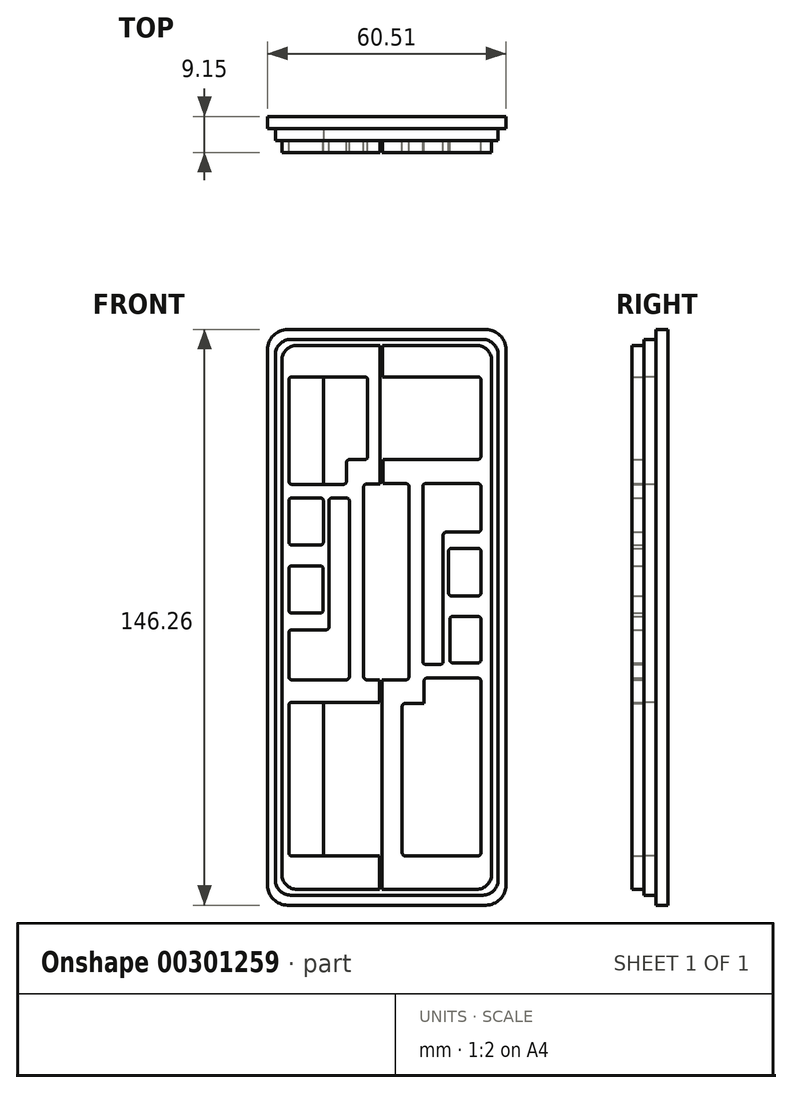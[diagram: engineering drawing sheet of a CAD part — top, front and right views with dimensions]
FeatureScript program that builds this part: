
annotation { "Feature Type Name" : "Feature", "Feature Type Description" : "" }
export const myFeature = defineFeature(function(context is Context, id is Id, definition is map)
    precondition{}
    {
        {
            var Q0;
            Q0=qCreatedBy(makeId("Front.planeOp"),FACE);
            var sketch = newSketch(context, id + "F0", { "sketchPlane" : qUnion([Q0])});
            skLineSegment(sketch, "E0", {"start": v(-27.22, -68.82) * mm, "end": v(-27.22, 61.78) * mm});
            skLineSegment(sketch, "E1", {"start": v(22.22, 65.6) * mm, "end": v(-23.4, 65.6) * mm});
            skLineSegment(sketch, "E2", {"start": v(22.22, -72.63) * mm, "end": v(-23.4, -72.63) * mm});
            skLineSegment(sketch, "E3", {"start": v(26.03, 61.78) * mm, "end": v(26.03, -68.82) * mm});
            skPoint(sketch, "E4.visualSharp", {"position": v(-27.22, 65.6) * mm});
            skArc(sketch, "E4.filletArc", {"start": v(-23.4, 65.6) * mm, "mid": v(-26.1, 64.48) * mm, "end": v(-27.22, 61.78) * mm});
            skPoint(sketch, "E5.visualSharp", {"position": v(26.03, 65.6) * mm});
            skArc(sketch, "E5.filletArc", {"start": v(26.03, 61.78) * mm, "mid": v(24.92, 64.48) * mm, "end": v(22.22, 65.6) * mm});
            skPoint(sketch, "E6.visualSharp", {"position": v(26.03, -72.63) * mm});
            skArc(sketch, "E6.filletArc", {"start": v(22.22, -72.63) * mm, "mid": v(24.92, -71.52) * mm, "end": v(26.03, -68.82) * mm});
            skPoint(sketch, "E7.visualSharp", {"position": v(-27.22, -72.63) * mm});
            skArc(sketch, "E7.filletArc", {"start": v(-27.22, -68.82) * mm, "mid": v(-26.1, -71.52) * mm, "end": v(-23.4, -72.63) * mm});
            skLineSegment(sketch, "E8", {"start": v(-24.7, -64.14) * mm, "end": v(-2.46, -64.14) * mm});
            skLineSegment(sketch, "E9", {"start": v(23.33, -63.38) * mm, "end": v(23.33, -19.72) * mm});
            skLineSegment(sketch, "E10", {"start": v(22.57, 57.59) * mm, "end": v(-1.65, 57.59) * mm});
            skLineSegment(sketch, "E11", {"start": v(-25.46, 56.82) * mm, "end": v(-25.46, 31.03) * mm});
            skLineSegment(sketch, "E12", {"start": v(-2.46, -25.08) * mm, "end": v(-24.7, -25.08) * mm});
            skLineSegment(sketch, "E13", {"start": v(-2.46, -25.08) * mm, "end": v(-2.46, -19.4) * mm});
            skLineSegment(sketch, "E14", {"start": v(-2.46, -19.4) * mm, "end": v(-5.7, -19.4) * mm});
            skLineSegment(sketch, "E15", {"start": v(-1.8, -19.4) * mm, "end": v(4.3, -19.4) * mm});
            skLineSegment(sketch, "E16", {"start": v(5.06, -18.63) * mm, "end": v(5.06, 29.68) * mm});
            skLineSegment(sketch, "E17", {"start": v(4.3, 30.44) * mm, "end": v(-1.52, 30.44) * mm});
            skLineSegment(sketch, "E18", {"start": v(-1.52, 30.44) * mm, "end": v(-1.52, 36.62) * mm});
            skLineSegment(sketch, "E19", {"start": v(-1.52, 36.62) * mm, "end": v(22.57, 36.62) * mm});
            skLineSegment(sketch, "E20", {"start": v(22.57, 30.47) * mm, "end": v(9.33, 30.47) * mm});
            skLineSegment(sketch, "E21", {"start": v(8.57, 29.71) * mm, "end": v(8.57, -14.73) * mm});
            skLineSegment(sketch, "E22", {"start": v(9.33, -15.49) * mm, "end": v(12.98, -15.49) * mm});
            skLineSegment(sketch, "E23", {"start": v(13.74, -14.73) * mm, "end": v(13.74, 17.36) * mm});
            skLineSegment(sketch, "E24", {"start": v(22.57, 14.02) * mm, "end": v(15.89, 14.02) * mm});
            skLineSegment(sketch, "E25", {"start": v(15.12, 13.26) * mm, "end": v(15.12, 2.68) * mm});
            skLineSegment(sketch, "E26", {"start": v(15.89, 1.92) * mm, "end": v(22.57, 1.92) * mm});
            skLineSegment(sketch, "E27", {"start": v(22.57, -3.28) * mm, "end": v(16.2, -3.28) * mm});
            skLineSegment(sketch, "E28", {"start": v(15.44, -4.04) * mm, "end": v(15.44, -14.33) * mm});
            skLineSegment(sketch, "E29", {"start": v(16.2, -15.1) * mm, "end": v(22.57, -15.1) * mm});
            skLineSegment(sketch, "E30", {"start": v(22.57, -18.96) * mm, "end": v(9.65, -18.96) * mm});
            skLineSegment(sketch, "E31", {"start": v(8.88, -19.72) * mm, "end": v(8.88, -25.38) * mm});
            skLineSegment(sketch, "E32", {"start": v(8.88, -25.38) * mm, "end": v(4.1, -25.38) * mm});
            skLineSegment(sketch, "E33", {"start": v(3.34, -26.14) * mm, "end": v(3.34, -63.38) * mm});
            skLineSegment(sketch, "E34", {"start": v(-1.8, -19.4) * mm, "end": v(-1.8, -72.63) * mm});
            skLineSegment(sketch, "E35", {"start": v(-2.46, -64.14) * mm, "end": v(-2.46, -72.63) * mm});
            skLineSegment(sketch, "E36.trimOffspring", {"start": v(4.1, -64.14) * mm, "end": v(22.57, -64.14) * mm});
            skLineSegment(sketch, "E37", {"start": v(-6.45, -18.63) * mm, "end": v(-6.45, 29.6) * mm});
            skLineSegment(sketch, "E38", {"start": v(-5.7, 30.36) * mm, "end": v(-2.29, 30.36) * mm});
            skLineSegment(sketch, "E39", {"start": v(-2.29, 30.36) * mm, "end": v(-2.29, 65.6) * mm});
            skLineSegment(sketch, "E40", {"start": v(-1.65, 65.6) * mm, "end": v(-1.65, 57.59) * mm});
            skPoint(sketch, "E40.endSnap0", {"position": v(-1.06, 57.59) * mm});
            skLineSegment(sketch, "E41.trimOffspring", {"start": v(-6.19, 57.59) * mm, "end": v(-24.7, 57.59) * mm});
            skLineSegment(sketch, "E42", {"start": v(-5.42, 56.82) * mm, "end": v(-5.42, 37.31) * mm});
            skLineSegment(sketch, "E43", {"start": v(-6.19, 36.55) * mm, "end": v(-10.06, 36.55) * mm});
            skLineSegment(sketch, "E44", {"start": v(-10.82, 35.79) * mm, "end": v(-10.82, 31.03) * mm});
            skLineSegment(sketch, "E45", {"start": v(-11.58, 30.27) * mm, "end": v(-24.7, 30.27) * mm});
            skLineSegment(sketch, "E46", {"start": v(-24.7, 26.82) * mm, "end": v(-17.45, 26.82) * mm});
            skLineSegment(sketch, "E47", {"start": v(-16.69, 26.06) * mm, "end": v(-16.69, 15.61) * mm});
            skLineSegment(sketch, "E48", {"start": v(-17.45, 14.85) * mm, "end": v(-24.7, 14.85) * mm});
            skLineSegment(sketch, "E49", {"start": v(-24.7, 9.56) * mm, "end": v(-17.51, 9.56) * mm});
            skLineSegment(sketch, "E50", {"start": v(-16.75, 8.8) * mm, "end": v(-16.75, -1.7) * mm});
            skLineSegment(sketch, "E51", {"start": v(-17.51, -2.46) * mm, "end": v(-24.7, -2.46) * mm});
            skLineSegment(sketch, "E52", {"start": v(-24.7, -6.7) * mm, "end": v(-16.03, -6.7) * mm});
            skLineSegment(sketch, "E53", {"start": v(-15.27, -5.94) * mm, "end": v(-15.27, 26.06) * mm});
            skLineSegment(sketch, "E54", {"start": v(-14.5, 26.82) * mm, "end": v(-10.86, 26.82) * mm});
            skLineSegment(sketch, "E55", {"start": v(-10.1, 26.06) * mm, "end": v(-10.1, -18.63) * mm});
            skLineSegment(sketch, "E56.trimOffspring", {"start": v(-10.86, -19.4) * mm, "end": v(-24.7, -19.4) * mm});
            skPoint(sketch, "E57.visualSharp", {"position": v(23.33, -64.14) * mm});
            skArc(sketch, "E57.filletArc", {"start": v(22.57, -64.14) * mm, "mid": v(23.1, -63.92) * mm, "end": v(23.33, -63.38) * mm});
            skPoint(sketch, "E58.visualSharp", {"position": v(3.34, -64.14) * mm});
            skArc(sketch, "E58.filletArc", {"start": v(3.34, -63.38) * mm, "mid": v(3.56, -63.92) * mm, "end": v(4.1, -64.14) * mm});
            skPoint(sketch, "E59.visualSharp", {"position": v(8.88, -18.96) * mm});
            skArc(sketch, "E59.filletArc", {"start": v(9.65, -18.96) * mm, "mid": v(9.1, -19.18) * mm, "end": v(8.88, -19.72) * mm});
            skPoint(sketch, "E60.newPointB", {"position": v(23.33, 57.59) * mm});
            skArc(sketch, "E60.filletArc", {"start": v(23.33, -19.72) * mm, "mid": v(23.1, -19.18) * mm, "end": v(22.57, -18.96) * mm});
            skPoint(sketch, "E61.visualSharp", {"position": v(3.34, -25.38) * mm});
            skArc(sketch, "E61.filletArc", {"start": v(4.1, -25.38) * mm, "mid": v(3.56, -25.6) * mm, "end": v(3.34, -26.14) * mm});
            skPoint(sketch, "E62.visualSharp", {"position": v(5.06, -19.4) * mm});
            skArc(sketch, "E62.filletArc", {"start": v(4.3, -19.4) * mm, "mid": v(4.84, -19.17) * mm, "end": v(5.06, -18.63) * mm});
            skPoint(sketch, "E63.visualSharp", {"position": v(8.57, -15.49) * mm});
            skArc(sketch, "E63.filletArc", {"start": v(8.57, -14.73) * mm, "mid": v(8.8, -15.26) * mm, "end": v(9.33, -15.49) * mm});
            skPoint(sketch, "E64.visualSharp", {"position": v(13.74, -15.49) * mm});
            skArc(sketch, "E64.filletArc", {"start": v(12.98, -15.49) * mm, "mid": v(13.51, -15.26) * mm, "end": v(13.74, -14.73) * mm});
            skPoint(sketch, "E65.visualSharp", {"position": v(15.44, -15.1) * mm});
            skArc(sketch, "E65.filletArc", {"start": v(15.44, -14.33) * mm, "mid": v(15.67, -14.87) * mm, "end": v(16.2, -15.1) * mm});
            skPoint(sketch, "E66.visualSharp", {"position": v(15.44, -3.28) * mm});
            skArc(sketch, "E66.filletArc", {"start": v(16.2, -3.28) * mm, "mid": v(15.67, -3.5) * mm, "end": v(15.44, -4.04) * mm});
            skPoint(sketch, "E67.visualSharp", {"position": v(15.12, 14.02) * mm});
            skArc(sketch, "E67.filletArc", {"start": v(15.89, 14.02) * mm, "mid": v(15.35, 13.8) * mm, "end": v(15.12, 13.26) * mm});
            skPoint(sketch, "E68.visualSharp", {"position": v(15.12, 1.92) * mm});
            skArc(sketch, "E68.filletArc", {"start": v(15.12, 2.68) * mm, "mid": v(15.35, 2.14) * mm, "end": v(15.89, 1.92) * mm});
            skPoint(sketch, "E69.visualSharp", {"position": v(8.57, 30.47) * mm});
            skArc(sketch, "E69.filletArc", {"start": v(9.33, 30.47) * mm, "mid": v(8.8, 30.25) * mm, "end": v(8.57, 29.71) * mm});
            skPoint(sketch, "E70.visualSharp", {"position": v(5.06, 30.44) * mm});
            skArc(sketch, "E70.filletArc", {"start": v(5.06, 29.68) * mm, "mid": v(4.84, 30.22) * mm, "end": v(4.3, 30.44) * mm});
            skPoint(sketch, "E71.visualSharp", {"position": v(-6.45, 30.36) * mm});
            skArc(sketch, "E71.filletArc", {"start": v(-5.7, 30.36) * mm, "mid": v(-6.23, 30.14) * mm, "end": v(-6.45, 29.6) * mm});
            skPoint(sketch, "E72.visualSharp", {"position": v(-10.1, 26.82) * mm});
            skArc(sketch, "E72.filletArc", {"start": v(-10.1, 26.06) * mm, "mid": v(-10.32, 26.6) * mm, "end": v(-10.86, 26.82) * mm});
            skPoint(sketch, "E73.visualSharp", {"position": v(-15.27, 26.82) * mm});
            skArc(sketch, "E73.filletArc", {"start": v(-14.5, 26.82) * mm, "mid": v(-15.04, 26.6) * mm, "end": v(-15.27, 26.06) * mm});
            skLineSegment(sketch, "E74", {"start": v(23.33, 56.82) * mm, "end": v(23.33, 37.38) * mm});
            skLineSegment(sketch, "E75.trimOffspring", {"start": v(23.33, -4.04) * mm, "end": v(23.33, -14.33) * mm});
            skLineSegment(sketch, "E76.trimOffspring", {"start": v(23.33, 29.71) * mm, "end": v(23.33, 18.88) * mm});
            skPoint(sketch, "E77.visualSharp", {"position": v(-16.69, 26.82) * mm});
            skArc(sketch, "E77.filletArc", {"start": v(-16.69, 26.06) * mm, "mid": v(-16.91, 26.6) * mm, "end": v(-17.45, 26.82) * mm});
            skPoint(sketch, "E78.visualSharp", {"position": v(-16.69, 14.85) * mm});
            skArc(sketch, "E78.filletArc", {"start": v(-17.45, 14.85) * mm, "mid": v(-16.91, 15.08) * mm, "end": v(-16.69, 15.61) * mm});
            skLineSegment(sketch, "E79.trimOffspring", {"start": v(-25.46, 8.8) * mm, "end": v(-25.46, -1.7) * mm});
            skLineSegment(sketch, "E80.trimOffspring", {"start": v(-25.46, 26.06) * mm, "end": v(-25.46, 15.61) * mm});
            skLineSegment(sketch, "E81.trimOffspring", {"start": v(-25.46, -7.46) * mm, "end": v(-25.46, -18.63) * mm});
            skLineSegment(sketch, "E82.trimOffspring", {"start": v(-25.46, -25.85) * mm, "end": v(-25.46, -63.38) * mm});
            skPoint(sketch, "E83.visualSharp", {"position": v(-25.46, -64.14) * mm});
            skArc(sketch, "E83.filletArc", {"start": v(-25.46, -63.38) * mm, "mid": v(-25.23, -63.92) * mm, "end": v(-24.7, -64.14) * mm});
            skPoint(sketch, "E84.visualSharp", {"position": v(-25.46, -25.08) * mm});
            skArc(sketch, "E84.filletArc", {"start": v(-24.7, -25.08) * mm, "mid": v(-25.23, -25.3) * mm, "end": v(-25.46, -25.85) * mm});
            skPoint(sketch, "E85.visualSharp", {"position": v(-6.45, -19.4) * mm});
            skArc(sketch, "E85.filletArc", {"start": v(-6.45, -18.63) * mm, "mid": v(-6.23, -19.17) * mm, "end": v(-5.7, -19.4) * mm});
            skPoint(sketch, "E86.visualSharp", {"position": v(-25.46, -19.4) * mm});
            skArc(sketch, "E86.filletArc", {"start": v(-25.46, -18.63) * mm, "mid": v(-25.23, -19.17) * mm, "end": v(-24.7, -19.4) * mm});
            skPoint(sketch, "E87.visualSharp", {"position": v(-10.1, -19.4) * mm});
            skArc(sketch, "E87.filletArc", {"start": v(-10.86, -19.4) * mm, "mid": v(-10.32, -19.17) * mm, "end": v(-10.1, -18.63) * mm});
            skPoint(sketch, "E88.visualSharp", {"position": v(-15.27, -6.7) * mm});
            skArc(sketch, "E88.filletArc", {"start": v(-16.03, -6.7) * mm, "mid": v(-15.49, -6.48) * mm, "end": v(-15.27, -5.94) * mm});
            skPoint(sketch, "E89.visualSharp", {"position": v(-25.46, -6.7) * mm});
            skArc(sketch, "E89.filletArc", {"start": v(-24.7, -6.7) * mm, "mid": v(-25.23, -6.92) * mm, "end": v(-25.46, -7.46) * mm});
            skPoint(sketch, "E90.visualSharp", {"position": v(-16.75, -2.46) * mm});
            skArc(sketch, "E90.filletArc", {"start": v(-17.51, -2.46) * mm, "mid": v(-16.97, -2.24) * mm, "end": v(-16.75, -1.7) * mm});
            skPoint(sketch, "E91.visualSharp", {"position": v(-25.46, -2.46) * mm});
            skArc(sketch, "E91.filletArc", {"start": v(-25.46, -1.7) * mm, "mid": v(-25.23, -2.24) * mm, "end": v(-24.7, -2.46) * mm});
            skPoint(sketch, "E92.visualSharp", {"position": v(-16.75, 9.56) * mm});
            skArc(sketch, "E92.filletArc", {"start": v(-16.75, 8.8) * mm, "mid": v(-16.97, 9.34) * mm, "end": v(-17.51, 9.56) * mm});
            skPoint(sketch, "E93.visualSharp", {"position": v(-25.46, 9.56) * mm});
            skArc(sketch, "E93.filletArc", {"start": v(-24.7, 9.56) * mm, "mid": v(-25.23, 9.34) * mm, "end": v(-25.46, 8.8) * mm});
            skPoint(sketch, "E94.visualSharp", {"position": v(-25.46, 14.85) * mm});
            skArc(sketch, "E94.filletArc", {"start": v(-25.46, 15.61) * mm, "mid": v(-25.23, 15.08) * mm, "end": v(-24.7, 14.85) * mm});
            skPoint(sketch, "E95.visualSharp", {"position": v(-25.46, 26.82) * mm});
            skArc(sketch, "E95.filletArc", {"start": v(-24.7, 26.82) * mm, "mid": v(-25.23, 26.6) * mm, "end": v(-25.46, 26.06) * mm});
            skPoint(sketch, "E96.visualSharp", {"position": v(-25.46, 57.59) * mm});
            skArc(sketch, "E96.filletArc", {"start": v(-24.7, 57.59) * mm, "mid": v(-25.23, 57.36) * mm, "end": v(-25.46, 56.82) * mm});
            skPoint(sketch, "E97.visualSharp", {"position": v(-5.42, 36.55) * mm});
            skArc(sketch, "E97.filletArc", {"start": v(-6.19, 36.55) * mm, "mid": v(-5.65, 36.77) * mm, "end": v(-5.42, 37.31) * mm});
            skPoint(sketch, "E98.visualSharp", {"position": v(-10.82, 30.27) * mm});
            skArc(sketch, "E98.filletArc", {"start": v(-11.58, 30.27) * mm, "mid": v(-11.04, 30.5) * mm, "end": v(-10.82, 31.03) * mm});
            skPoint(sketch, "E99.visualSharp", {"position": v(-25.46, 30.27) * mm});
            skArc(sketch, "E99.filletArc", {"start": v(-25.46, 31.03) * mm, "mid": v(-25.23, 30.5) * mm, "end": v(-24.7, 30.27) * mm});
            skPoint(sketch, "E100.visualSharp", {"position": v(-10.82, 36.55) * mm});
            skArc(sketch, "E100.filletArc", {"start": v(-10.06, 36.55) * mm, "mid": v(-10.6, 36.33) * mm, "end": v(-10.82, 35.79) * mm});
            skArc(sketch, "E101.filletArc", {"start": v(23.33, 56.82) * mm, "mid": v(23.1, 57.36) * mm, "end": v(22.57, 57.59) * mm});
            skPoint(sketch, "E102.visualSharp", {"position": v(23.33, 36.62) * mm});
            skArc(sketch, "E102.filletArc", {"start": v(22.57, 36.62) * mm, "mid": v(23.1, 36.84) * mm, "end": v(23.33, 37.38) * mm});
            skPoint(sketch, "E103.visualSharp", {"position": v(23.33, 30.47) * mm});
            skArc(sketch, "E103.filletArc", {"start": v(23.33, 29.71) * mm, "mid": v(23.1, 30.25) * mm, "end": v(22.57, 30.47) * mm});
            skPoint(sketch, "E104.visualSharp", {"position": v(23.33, 1.92) * mm});
            skArc(sketch, "E104.filletArc", {"start": v(22.57, 1.92) * mm, "mid": v(23.1, 2.14) * mm, "end": v(23.33, 2.68) * mm});
            skLineSegment(sketch, "E105", {"start": v(14.5, 18.12) * mm, "end": v(22.57, 18.12) * mm});
            skLineSegment(sketch, "E106.trimOffspring", {"start": v(23.33, 13.26) * mm, "end": v(23.33, 2.68) * mm});
            skPoint(sketch, "E107.visualSharp", {"position": v(-5.42, 57.59) * mm});
            skArc(sketch, "E107.filletArc", {"start": v(-5.42, 56.82) * mm, "mid": v(-5.65, 57.36) * mm, "end": v(-6.19, 57.59) * mm});
            skPoint(sketch, "E108.visualSharp", {"position": v(13.74, 18.12) * mm});
            skArc(sketch, "E108.filletArc", {"start": v(14.5, 18.12) * mm, "mid": v(13.96, 17.9) * mm, "end": v(13.74, 17.36) * mm});
            skPoint(sketch, "E109.visualSharp", {"position": v(23.33, 18.12) * mm});
            skArc(sketch, "E109.filletArc", {"start": v(22.57, 18.12) * mm, "mid": v(23.1, 18.34) * mm, "end": v(23.33, 18.88) * mm});
            skPoint(sketch, "E110.visualSharp", {"position": v(23.33, 14.02) * mm});
            skArc(sketch, "E110.filletArc", {"start": v(23.33, 13.26) * mm, "mid": v(23.1, 13.8) * mm, "end": v(22.57, 14.02) * mm});
            skPoint(sketch, "E111.visualSharp", {"position": v(23.33, -3.28) * mm});
            skArc(sketch, "E111.filletArc", {"start": v(23.33, -4.04) * mm, "mid": v(23.1, -3.5) * mm, "end": v(22.57, -3.28) * mm});
            skPoint(sketch, "E112.visualSharp", {"position": v(23.33, -15.1) * mm});
            skArc(sketch, "E112.filletArc", {"start": v(22.57, -15.1) * mm, "mid": v(23.1, -14.87) * mm, "end": v(23.33, -14.33) * mm});
            skSolve(sketch);
        }
        {
            var Q0;
            Q0=makeQuery(id+"F0.imprint","IMPRINT",FACE,{"disambiguationData":[TD([[makeQuery(id+"F0.imprint","IMPRINT",EDGE,{"derivedFrom":sQuery(id+"F0.wireOp",EDGE,"E0")}),-1.0]])]});
            var Q1;
            Q1=makeQuery(id+"F0.imprint","IMPRINT",FACE,{"disambiguationData":[TD([[makeQuery(id+"F0.imprint","IMPRINT",EDGE,{"derivedFrom":sQuery(id+"F0.wireOp",EDGE,"E3")}),-1.0]])]});
            extrude(context, id + "F1", {"entities" : qUnion([Q0, Q1]), "depth" : 3.05 * mm});
        }
        {
            var Q0;
            Q0=qCreatedBy(makeId("Front.planeOp"),FACE);
            var sketch = newSketch(context, id + "F2", { "sketchPlane" : qUnion([Q0])});
            skLineSegment(sketch, "E113.0", {"start": v(23.87, -74.1) * mm, "end": v(-25.06, -74.1) * mm});
            skLineSegment(sketch, "E113.1", {"start": v(23.87, 67.07) * mm, "end": v(-25.06, 67.07) * mm});
            skLineSegment(sketch, "E113.3", {"start": v(-28.87, -70.3) * mm, "end": v(-28.87, 63.26) * mm});
            skLineSegment(sketch, "E114", {"start": v(27.68, -70.3) * mm, "end": v(27.68, 63.26) * mm});
            skPoint(sketch, "E115.visualSharp", {"position": v(-28.87, -74.1) * mm});
            skArc(sketch, "E115.filletArc", {"start": v(-28.87, -70.3) * mm, "mid": v(-27.75, -72.99) * mm, "end": v(-25.06, -74.1) * mm});
            skPoint(sketch, "E116.visualSharp", {"position": v(27.68, -74.1) * mm});
            skArc(sketch, "E116.filletArc", {"start": v(23.87, -74.1) * mm, "mid": v(26.57, -72.99) * mm, "end": v(27.68, -70.3) * mm});
            skPoint(sketch, "E117.visualSharp", {"position": v(27.68, 67.07) * mm});
            skArc(sketch, "E117.filletArc", {"start": v(27.68, 63.26) * mm, "mid": v(26.57, 65.95) * mm, "end": v(23.87, 67.07) * mm});
            skPoint(sketch, "E118.visualSharp", {"position": v(-28.87, 67.07) * mm});
            skArc(sketch, "E118.filletArc", {"start": v(-25.06, 67.07) * mm, "mid": v(-27.75, 65.95) * mm, "end": v(-28.87, 63.26) * mm});
            skLineSegment(sketch, "E119.0", {"start": v(-24.7, -64.14) * mm, "end": v(-16.71, -64.14) * mm});
            skLineSegment(sketch, "E120.0", {"start": v(-25.46, -25.85) * mm, "end": v(-25.46, -63.38) * mm});
            skArc(sketch, "E120.1", {"start": v(-25.46, -63.38) * mm, "mid": v(-25.23, -63.92) * mm, "end": v(-24.7, -64.14) * mm});
            skArc(sketch, "E121.0", {"start": v(-24.7, -25.08) * mm, "mid": v(-25.23, -25.3) * mm, "end": v(-25.46, -25.85) * mm});
            skLineSegment(sketch, "E121.1", {"start": v(-16.71, -25.08) * mm, "end": v(-24.7, -25.08) * mm});
            skLineSegment(sketch, "E122.0", {"start": v(-16.71, 30.27) * mm, "end": v(-24.7, 30.27) * mm});
            skArc(sketch, "E122.1", {"start": v(-25.46, 31.03) * mm, "mid": v(-25.23, 30.5) * mm, "end": v(-24.7, 30.27) * mm});
            skLineSegment(sketch, "E122.2", {"start": v(-25.46, 56.82) * mm, "end": v(-25.46, 31.03) * mm});
            skLineSegment(sketch, "E122.3", {"start": v(-16.71, 57.59) * mm, "end": v(-24.7, 57.59) * mm});
            skArc(sketch, "E122.4", {"start": v(-24.7, 57.59) * mm, "mid": v(-25.23, 57.36) * mm, "end": v(-25.46, 56.82) * mm});
            skLineSegment(sketch, "E123", {"start": v(-16.71, 57.59) * mm, "end": v(-16.71, 30.27) * mm});
            skPoint(sketch, "E124.orphan", {"position": v(-2.46, -64.14) * mm});
            skPoint(sketch, "E125.orphan", {"position": v(-2.46, -25.08) * mm});
            skLineSegment(sketch, "E126.trimOffspring", {"start": v(-16.71, -25.08) * mm, "end": v(-16.71, -64.14) * mm});
            skPoint(sketch, "E127.orphan", {"position": v(-11.58, 30.27) * mm});
            skPoint(sketch, "E128.orphan", {"position": v(-6.19, 57.59) * mm});
            skSolve(sketch);
        }
        {
            var Q0;
            Q0 = qSketchRegion(id + "F2", true);
            extrude(context, id + "F3", {"entities" : qUnion([Q0]), "operationType" : NewBodyOperationType.ADD, "oppositeDirection" : true, "depth" : 3.05 * mm});
        }
        {
            var Q0;
            Q0=makeQuery(id+"F3.opExtrude","CAP_FACE",FACE,{"disambiguationData":[OSD([sQuery(id+"F2.wireOp",EDGE,"E113.0"),sQuery(id+"F2.wireOp",EDGE,"E113.1"),sQuery(id+"F2.wireOp",EDGE,"E113.3"),sQuery(id+"F2.wireOp",EDGE,"E114"),sQuery(id+"F2.wireOp",EDGE,"E115.filletArc"),sQuery(id+"F2.wireOp",EDGE,"E116.filletArc"),sQuery(id+"F2.wireOp",EDGE,"E117.filletArc"),sQuery(id+"F2.wireOp",EDGE,"E118.filletArc"),sQuery(id+"F2.wireOp",EDGE,"E119.0"),sQuery(id+"F2.wireOp",EDGE,"E120.0"),sQuery(id+"F2.wireOp",EDGE,"E120.1"),sQuery(id+"F2.wireOp",EDGE,"E121.0"),sQuery(id+"F2.wireOp",EDGE,"E121.1"),sQuery(id+"F2.wireOp",EDGE,"E122.0"),sQuery(id+"F2.wireOp",EDGE,"E122.1"),sQuery(id+"F2.wireOp",EDGE,"E122.2"),sQuery(id+"F2.wireOp",EDGE,"E122.3"),sQuery(id+"F2.wireOp",EDGE,"E122.4"),sQuery(id+"F2.wireOp",EDGE,"E123"),sQuery(id+"F2.wireOp",EDGE,"E126.trimOffspring")])],"isStart":false});
            var sketch = newSketch(context, id + "F4", { "sketchPlane" : qUnion([Q0])});
            skLineSegment(sketch, "E129", {"start": v(-29.66, -71.57) * mm, "end": v(-29.66, 64.53) * mm});
            skLineSegment(sketch, "E130", {"start": v(-24.58, 69.6) * mm, "end": v(25.77, 69.6) * mm});
            skLineSegment(sketch, "E131", {"start": v(30.85, 64.53) * mm, "end": v(30.85, -71.57) * mm});
            skLineSegment(sketch, "E132", {"start": v(25.77, -76.65) * mm, "end": v(-24.58, -76.65) * mm});
            skPoint(sketch, "E133.visualSharp", {"position": v(-29.66, 69.6) * mm});
            skArc(sketch, "E133.filletArc", {"start": v(-24.58, 69.6) * mm, "mid": v(-28.18, 68.12) * mm, "end": v(-29.66, 64.53) * mm});
            skPoint(sketch, "E134.visualSharp", {"position": v(30.85, 69.6) * mm});
            skArc(sketch, "E134.filletArc", {"start": v(30.85, 64.53) * mm, "mid": v(29.36, 68.12) * mm, "end": v(25.77, 69.6) * mm});
            skPoint(sketch, "E135.visualSharp", {"position": v(30.85, -76.65) * mm});
            skArc(sketch, "E135.filletArc", {"start": v(25.77, -76.65) * mm, "mid": v(29.36, -75.16) * mm, "end": v(30.85, -71.57) * mm});
            skPoint(sketch, "E136.visualSharp", {"position": v(-29.66, -76.65) * mm});
            skArc(sketch, "E136.filletArc", {"start": v(-29.66, -71.57) * mm, "mid": v(-28.18, -75.16) * mm, "end": v(-24.58, -76.65) * mm});
            skSolve(sketch);
        }
        {
            var Q0;
            Q0 = qSketchRegion(id + "F4", true);
            extrude(context, id + "F5", {"entities" : qUnion([Q0]), "operationType" : NewBodyOperationType.ADD, "depth" : 3.05 * mm});
        }
    });
